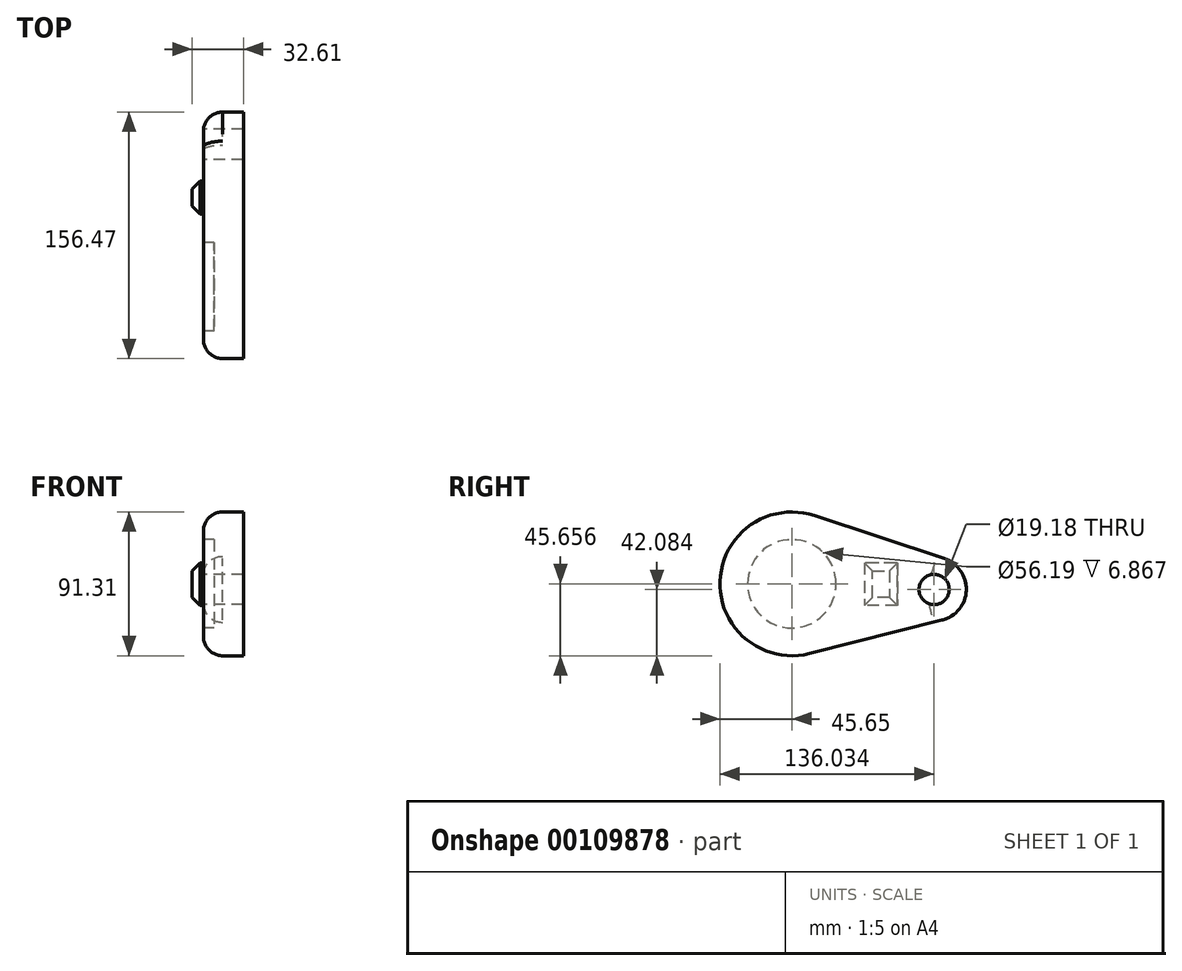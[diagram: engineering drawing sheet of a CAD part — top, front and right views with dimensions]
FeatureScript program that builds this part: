
annotation { "Feature Type Name" : "Feature", "Feature Type Description" : "" }
export const myFeature = defineFeature(function(context is Context, id is Id, definition is map)
    precondition{}
    {
        {
            var Q0;
            Q0=qCreatedBy(makeId("Right.planeOp"),FACE);
            var sketch = newSketch(context, id + "F0", { "sketchPlane" : qUnion([Q0])});
            skCircle(sketch, "E0", {"center": v(-63.66, 19.44) * mm, "radius": 45.65 * mm});
            skCircle(sketch, "E1", {"center": v(26.81, 16.15) * mm, "radius": 20.34 * mm});
            skLineSegment(sketch, "E2", {"start": v(33.2, 35.46) * mm, "end": v(-49.31, 62.78) * mm});
            skLineSegment(sketch, "E3", {"start": v(-52.5, -24.83) * mm, "end": v(31.79, -3.58) * mm});
            skSolve(sketch);
        }
        {
            var Q0;
            Q0 = qSketchRegion(id + "F0", true);
            extrude(context, id + "F1", {"entities" : qUnion([Q0]), "depth" : 25.4 * mm});
        }
        {
            var Q0;
            Q0=makeQuery(id+"F1.opExtrude","CAP_FACE",FACE,{"disambiguationData":[OSD([sQuery(id+"F0.wireOp",EDGE,"E0"),sQuery(id+"F0.wireOp",EDGE,"E1"),sQuery(id+"F0.wireOp",EDGE,"E2"),sQuery(id+"F0.wireOp",EDGE,"E3")])],"isStart":true});
            var sketch = newSketch(context, id + "F2", { "sketchPlane" : qUnion([Q0])});
            skCircle(sketch, "E4", {"center": v(63.66, 19.44) * mm, "radius": 28.1 * mm});
            skSolve(sketch);
        }
        {
            var Q0;
            {var subQ0=sQuery(id+"F0.wireOp",EDGE,"E1");var subQ1=makeQuery(id+"F0.imprint","INTERSECT",VERTEX,{"derivedFrom":[subQ0,sQuery(id+"F0.wireOp",EDGE,"E2")]});Q0=makeQuery(id+"F0.imprint","IMPRINT",FACE,{"disambiguationData":[TD([[makeQuery(id+"F0.imprint","IMPRINT",EDGE,{"disambiguationData":[TD([[subQ1,-1.0]])],"derivedFrom":subQ0}),1.0]])]});}
            var sketch = newSketch(context, id + "F3", { "sketchPlane" : qUnion([Q0])});
            skCircle(sketch, "E5", {"center": v(26.72, 15.86) * mm, "radius": 9.59 * mm});
            skSolve(sketch);
        }
        {
            var Q0;
            Q0 = qSketchRegion(id + "F3", true);
            extrude(context, id + "F4", {"entities" : qUnion([Q0]), "operationType" : NewBodyOperationType.REMOVE, "depth" : 25.4 * mm});
        }
        {
            var Q0;
            Q0 = qSketchRegion(id + "F2", true);
            extrude(context, id + "F5", {"entities" : qUnion([Q0]), "operationType" : NewBodyOperationType.REMOVE, "oppositeDirection" : true, "depth" : 6.87 * mm});
        }
        {
            var Q0;
            {var subQ0=sQuery(id+"F0.wireOp",EDGE,"E2");Q0=makeQuery(id+"F0.imprint","IMPRINT",FACE,{"disambiguationData":[TD([[makeQuery(id+"F0.imprint","IMPRINT",EDGE,{"derivedFrom":subQ0}),1.0]])]});}
            var sketch = newSketch(context, id + "F6", { "sketchPlane" : qUnion([Q0])});
            skLineSegment(sketch, "E6.bottom", {"start": v(3.27, 32.76) * mm, "end": v(-17.42, 32.76) * mm});
            skLineSegment(sketch, "E6.top", {"start": v(3.27, 5.86) * mm, "end": v(-17.42, 5.86) * mm});
            skLineSegment(sketch, "E6.left", {"start": v(3.27, 32.76) * mm, "end": v(3.27, 5.86) * mm});
            skLineSegment(sketch, "E6.right", {"start": v(-17.42, 32.76) * mm, "end": v(-17.42, 5.86) * mm});
            skSolve(sketch);
        }
        {
            var Q0;
            Q0 = qSketchRegion(id + "F6", true);
            extrude(context, id + "F7", {"entities" : qUnion([Q0]), "operationType" : NewBodyOperationType.ADD, "oppositeDirection" : true, "depth" : 7.2 * mm});
        }
        {
            var Q0;
            Q0=makeQuery(id+"F1.opExtrude","CAP_EDGE",EDGE,{"disambiguationData":[OSD([sQuery(id+"F0.wireOp",EDGE,"E1")])],"isStart":true});
            fillet(context, id + "F8", {"entities" : qUnion([Q0]), "radius" : 12.3 * mm, "tangentPropagation" : true, "allowEdgeOverflow" : false});
        }
        {
            var Q0;
            Q0=makeQuery(id+"F7.opExtrude","CAP_FACE",FACE,{"disambiguationData":[OSD([sQuery(id+"F6.wireOp",EDGE,"E6.bottom"),sQuery(id+"F6.wireOp",EDGE,"E6.top"),sQuery(id+"F6.wireOp",EDGE,"E6.left"),sQuery(id+"F6.wireOp",EDGE,"E6.right")])],"isStart":false});
            chamfer(context, id + "F9", {"entities" : qUnion([Q0]), "width" : 5.08 * mm, "tangentPropagation" : true});
        }
    });
